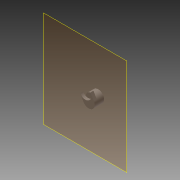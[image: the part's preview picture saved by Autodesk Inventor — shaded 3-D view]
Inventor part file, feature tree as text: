
AUTODESK INVENTOR PART (.ipt)
format: ipt  version: 2015 SP1 (Build 190203100, 203)  size: 92,672 bytes
history: native  units: in
note: dims shown in document units (in); Inventor stores cm internally (conversion verified against a paired STEP export)
features: extrude x2, sketch x2, reference x2, plane x1
ambient origin geometry x8: Origin, YZ Plane, XZ Plane, XY Plane, X Axis, Y Axis, Z Axis, Center Point
bodies: Solid1 (feature_tree)
feature tree (7):
  plane  "Work Plane1"
  extrude  "Extrusion1"  Depth=0.3543in TaperAngle=0.0deg
  extrude  "Extrusion3"  [1 undecoded]
  sketch  "Sketch1"  dims[d0=0.1575in d1=0.0in d4=0.3543in d5=0.0in]
  reference  "Reference1"
  reference  "Reference2"
  sketch  "Sketch2"
note: 1 required parameter value undecoded (feature->parameter linkage not recoverable at this tier; creation-order binding heuristic only, values carry confidence <= 0.55)
